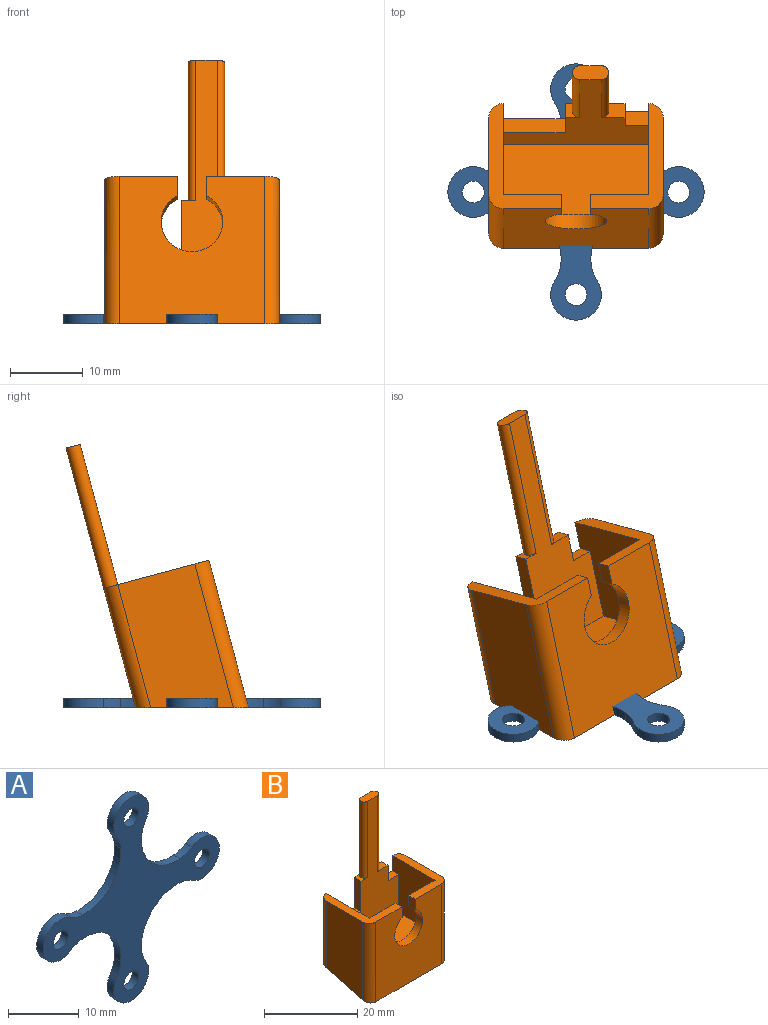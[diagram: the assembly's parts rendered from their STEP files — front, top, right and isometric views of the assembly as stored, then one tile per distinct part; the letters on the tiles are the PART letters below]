
ASSEMBLY  parts=2 mates=1
PART A: 22 faces, bbox 35.3x1.3x35.3 mm
  f0: cylinder r=5mm len=2.39mm, axis (0,1,0), area 3.3mm2, adj f1,f19,f20,f21
  f1: cylinder r=3.5mm len=7mm, axis (0,1,0), area 19.7mm2, adj f0,f2,f20,f21
  f2: cylinder r=5mm len=2.39mm, axis (0,1,0), area 3.3mm2, adj f1,f3,f20,f21
  f3: cylinder r=7.18mm len=7.75mm, axis (0,1,0), area 16.1mm2, adj f2,f4,f20,f21
  f4: cylinder r=5mm len=2.39mm, axis (0,1,0), area 3.3mm2, adj f3,f5,f20,f21
  f5: cylinder r=3.5mm len=7mm, axis (0,1,0), area 19.7mm2, adj f4,f6,f20,f21
  f6: cylinder r=5mm len=2.39mm, axis (0,1,0), area 3.3mm2, adj f5,f7,f20,f21
  f7: cylinder r=7.18mm len=7.75mm, axis (0,1,0), area 16.1mm2, adj f6,f8,f20,f21
  f8: cylinder r=5mm len=2.39mm, axis (0,1,0), area 3.3mm2, adj f7,f9,f20,f21
  f9: cylinder r=3.5mm len=7mm, axis (0,1,0), area 19.7mm2, adj f8,f10,f20,f21
  f10: cylinder r=5mm len=2.39mm, axis (0,1,0), area 3.3mm2, adj f9,f11,f20,f21
  f11: cylinder r=7.18mm len=7.75mm, axis (0,1,0), area 16.1mm2, adj f10,f12,f20,f21
  f12: cylinder r=5mm len=2.39mm, axis (0,1,0), area 3.3mm2, adj f11,f13,f20,f21
  f13: cylinder r=3.5mm len=7mm, axis (0,1,0), area 19.7mm2, adj f12,f14,f20,f21
  f14: cylinder r=5mm len=2.39mm, axis (0,1,0), area 3.3mm2, adj f13,f19,f20,f21
  f15: cylinder r=1.5mm len=3mm, axis (0,1,0), area 12.3mm2, adj f20,f21
  f16: cylinder r=1.5mm len=3mm, axis (0,1,0), area 12.3mm2, adj f20,f21
  f17: cylinder r=1.5mm len=3mm, axis (0,1,0), area 12.3mm2, adj f20,f21
  f18: cylinder r=1.5mm len=3mm, axis (0,1,0), area 12.3mm2, adj f20,f21
  f19: cylinder r=7.18mm len=7.75mm, axis (0,1,0), area 16.1mm2, adj f0,f14,f20,f21
  f20: plane 35.28x35.28mm, normal (0,-1,0), area 333.8mm2, adj f0,f1,f2,f3,f4,f5,f6,f7
  f21: plane 35.28x35.28mm, normal (0,1,0), area 333.8mm2, adj f0,f1,f2,f3,f4,f5,f6,f7
PART B: 28 faces, bbox 24x15x41 mm
  f0: plane 36.98x20mm, normal (0,1,0), area 318.6mm2, adj f2,f3,f7,f9,f20,f21,f22,f23
  f1: plane 20.46x11mm, normal (-1,0,0), area 208.9mm2, adj f3,f4,f8,f27
  f2: cylinder r=2mm len=17.52mm, axis (0,0,-1), area 54mm2, adj f0,f10,f11,f13,f27
  f3: cylinder r=2mm len=17.52mm, axis (0,0,1), area 54mm2, adj f0,f1,f8,f14,f27
  f4: cylinder r=2mm len=21mm, axis (0,0,-1), area 65.4mm2, adj f1,f8,f12,f27
  f5: cylinder r=2mm len=21mm, axis (0,0,1), area 65.4mm2, adj f10,f11,f12,f27
  f6: plane 34x20mm, normal (0,-1,0), area 259mm2, adj f7,f9,f13,f14,f16,f20,f21,f22
  f7: plane 3.25x2mm, normal (0,0,1), area 4.9mm2, adj f0,f6,f21,f25
  f8: plane 15x10mm, normal (0,0,1), area 44.3mm2, adj f1,f3,f4,f12,f14,f15,f19
  f9: plane 2x2mm, normal (0,0,1), area 2.4mm2, adj f0,f6,f22,f23
  f10: plane 15x10mm, normal (0,0,1), area 44.3mm2, adj f2,f5,f11,f12,f13,f15,f18
  f11: plane 20.46x11mm, normal (1,0,0), area 208.9mm2, adj f2,f5,f10,f27
  f12: plane 21x20mm, normal (0,-1,0), area 353.6mm2, adj f4,f5,f8,f10,f17,f18,f19,f27
  f13: plane 14x13mm, normal (-1,0,0), area 162mm2, adj f2,f6,f10,f15,f16,f26
  f14: plane 14x13mm, normal (1,0,0), area 170mm2, adj f3,f6,f8,f15,f16,f24
  f15: plane 20x14mm, normal (0,1,0), area 213.6mm2, adj f8,f10,f13,f14,f16,f17,f18,f19
  f16: plane 20x11mm, normal (0,0,1), area 220mm2, adj f6,f13,f14,f15
  f17: cylinder r=4.25mm len=8.5mm, axis (0,-1,0), area 45.1mm2, adj f12,f15,f18,f19
  f18: plane 2.75x2mm, normal (-1,0,0), area 5.5mm2, adj f10,f12,f15,f17
  f19: plane 2.75x2mm, normal (1,0,0), area 5.5mm2, adj f8,f12,f15,f17
  f20: plane 5x2mm, normal (0,0,1), area 9.1mm2, adj f0,f6,f21,f22
  f21: cylinder r=1mm len=20mm, axis (0,0,-1), area 62.8mm2, adj f0,f6,f7,f20
  f22: cylinder r=1mm len=20mm, axis (0,0,1), area 62.8mm2, adj f0,f6,f9,f20
  f23: plane 8x2mm, normal (-1,0,0), area 16mm2, adj f0,f6,f9,f24
  f24: plane 8.5x2mm, normal (0,0,1), area 17mm2, adj f0,f6,f14,f23
  f25: plane 4x2mm, normal (1,0,0), area 8mm2, adj f0,f6,f7,f26
  f26: plane 3.25x2mm, normal (0,0,1), area 6.5mm2, adj f0,f6,f13,f25
  f27: plane 24x15mm, normal (0,0.26,-0.97), area 369.1mm2, adj f0,f1,f2,f3,f4,f5,f11,f12
PLACE A rot(axis=(1,0,0),90deg) t=(0,-53.44,57.53)mm
PLACE B rot(axis=(-1,0,0),15deg) t=(0,-52.66,59.12)mm
MATE fastened B.f27 <-> A.f20  axis (0,0,-1) through (0,-53.44,56.23)mm
